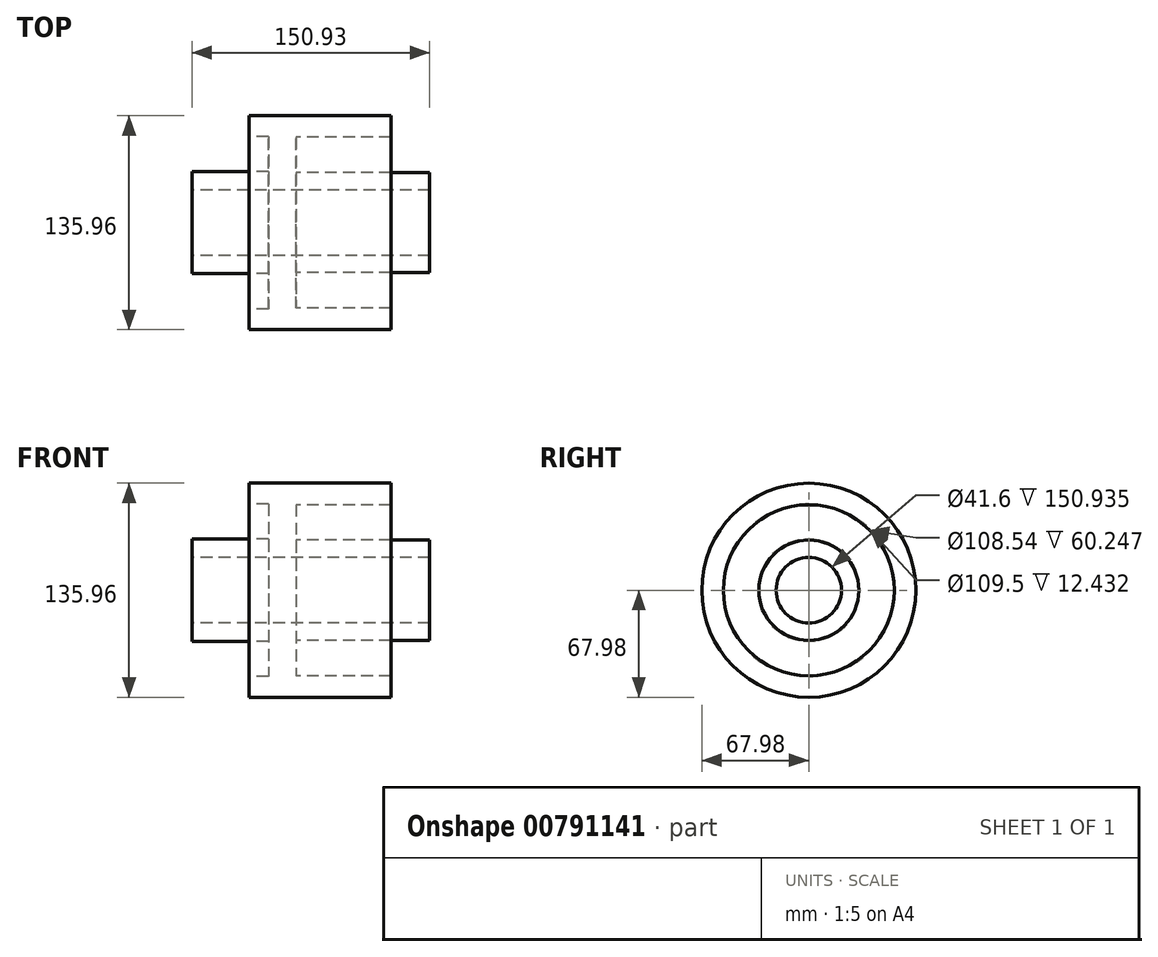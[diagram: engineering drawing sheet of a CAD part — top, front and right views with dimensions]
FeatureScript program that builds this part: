
annotation { "Feature Type Name" : "Feature", "Feature Type Description" : "" }
export const myFeature = defineFeature(function(context is Context, id is Id, definition is map)
    precondition{}
    {
        {
            var Q0;
            Q0=qCreatedBy(makeId("Front.planeOp"),FACE);
            var sketch = newSketch(context, id + "F0", { "sketchPlane" : qUnion([Q0])});
            skLineSegment(sketch, "E0", {"start": v(0, 0) * mm, "end": v(112.32, 0) * mm, "construction": true});
            skLineSegment(sketch, "E1", {"start": v(-55.5, 20.8) * mm, "end": v(95.44, 20.8) * mm});
            skLineSegment(sketch, "E2", {"start": v(95.44, 20.8) * mm, "end": v(95.44, 31.8) * mm});
            skLineSegment(sketch, "E3", {"start": v(95.44, 31.8) * mm, "end": v(10.65, 31.8) * mm});
            skLineSegment(sketch, "E4", {"start": v(10.65, 31.8) * mm, "end": v(10.65, 54.27) * mm});
            skLineSegment(sketch, "E5", {"start": v(10.65, 54.27) * mm, "end": v(70.9, 54.27) * mm});
            skLineSegment(sketch, "E6", {"start": v(70.9, 54.27) * mm, "end": v(70.9, 67.98) * mm});
            skLineSegment(sketch, "E7", {"start": v(70.9, 67.98) * mm, "end": v(-19.31, 67.98) * mm});
            skLineSegment(sketch, "E8", {"start": v(-19.31, 67.98) * mm, "end": v(-19.31, 54.75) * mm});
            skLineSegment(sketch, "E9", {"start": v(-19.31, 54.75) * mm, "end": v(-6.88, 54.75) * mm});
            skLineSegment(sketch, "E10", {"start": v(-6.88, 54.75) * mm, "end": v(-6.88, 32.43) * mm});
            skLineSegment(sketch, "E11", {"start": v(-6.88, 32.43) * mm, "end": v(-55.5, 32.43) * mm});
            skLineSegment(sketch, "E12", {"start": v(-55.5, 32.43) * mm, "end": v(-55.5, 20.8) * mm});
            skLineSegment(sketch, "E13", {"start": v(0, 0) * mm, "end": v(0, 78.66) * mm, "construction": true});
            skSolve(sketch);
        }
        {
            var Q0;
            Q0=makeQuery(id+"F0.imprint","IMPRINT",FACE,{"disambiguationData":[TD([[makeQuery(id+"F0.imprint","IMPRINT",EDGE,{"derivedFrom":sQuery(id+"F0.wireOp",EDGE,"E1")}),1.0]])]});
            var Q1;
            Q1=sQuery(id+"F0.wireOp",EDGE,"E0");
            revolve(context, id + "F1", {"surfaceOperationType" : NewSurfaceOperationType.NEW, "entities" : qUnion([Q0]), "axis" : qUnion([Q1]), "revolveType" : RevolveType.FULL});
        }
    });
